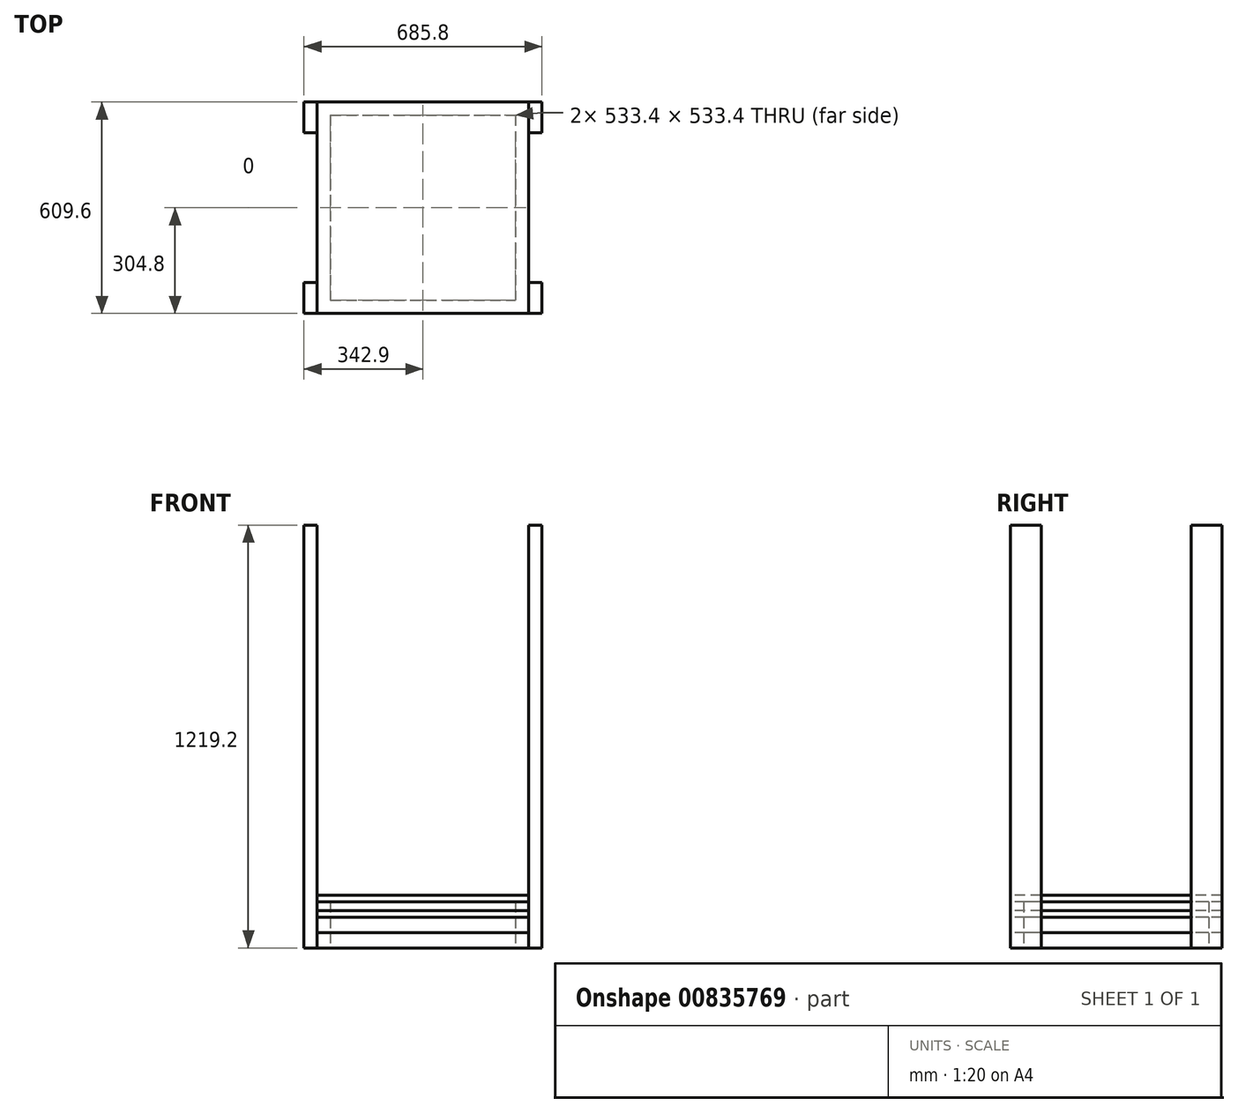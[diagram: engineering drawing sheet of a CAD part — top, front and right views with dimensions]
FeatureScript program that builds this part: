
annotation { "Feature Type Name" : "Feature", "Feature Type Description" : "" }
export const myFeature = defineFeature(function(context is Context, id is Id, definition is map)
    precondition{}
    {
        {
            var Q0;
            Q0=qCreatedBy(makeId("Top.planeOp"),FACE);
            var sketch = newSketch(context, id + "F0", { "sketchPlane" : qUnion([Q0])});
            skLineSegment(sketch, "E0.top", {"start": v(304.8, -304.8) * mm, "end": v(-304.8, -304.8) * mm, "construction": true});
            skPoint(sketch, "E0.middle", {"position": v(0, 0) * mm});
            skLineSegment(sketch, "E1.bottom", {"start": v(-304.8, 304.8) * mm, "end": v(304.8, 304.8) * mm});
            skLineSegment(sketch, "E1.top", {"start": v(-266.7, 266.7) * mm, "end": v(266.7, 266.7) * mm});
            skLineSegment(sketch, "E2.0.1.0", {"start": v(-266.7, -266.7) * mm, "end": v(266.7, -266.7) * mm});
            skLineSegment(sketch, "E2.0.1.3", {"start": v(-304.8, -304.8) * mm, "end": v(304.8, -304.8) * mm});
            skLineSegment(sketch, "E2.1.0.0", {"start": v(-279.4, 304.8) * mm, "end": v(304.8, 304.8) * mm});
            skLineSegment(sketch, "E2.1.1.0", {"start": v(-266.7, -266.7) * mm, "end": v(304.8, -266.7) * mm});
            skLineSegment(sketch, "E2.1.1.3", {"start": v(-279.4, -304.8) * mm, "end": v(304.8, -304.8) * mm});
            skPoint(sketch, "E3.orphan", {"position": v(330.2, 266.7) * mm});
            skPoint(sketch, "E4.orphan", {"position": v(330.2, -304.8) * mm});
            skLineSegment(sketch, "E5.bottom", {"start": v(-304.8, 304.8) * mm, "end": v(-266.7, 304.8) * mm});
            skLineSegment(sketch, "E5.left", {"start": v(-304.8, 215.9) * mm, "end": v(-304.8, -215.9) * mm});
            skLineSegment(sketch, "E5.right", {"start": v(-266.7, 266.7) * mm, "end": v(-266.7, -266.7) * mm});
            skLineSegment(sketch, "E6.MirrorCS", {"start": v(266.7, 266.7) * mm, "end": v(266.7, -266.7) * mm});
            skLineSegment(sketch, "E7.MirrorCS", {"start": v(304.8, 215.9) * mm, "end": v(304.8, -215.9) * mm});
            skPoint(sketch, "E8.orphan", {"position": v(266.7, 304.8) * mm});
            skPoint(sketch, "E9.orphan", {"position": v(304.8, 304.8) * mm});
            skPoint(sketch, "E10.orphan", {"position": v(304.8, -266.7) * mm});
            skPoint(sketch, "E11.orphan", {"position": v(-304.8, -266.7) * mm});
            skLineSegment(sketch, "E12", {"start": v(-304.8, 304.8) * mm, "end": v(-304.8, 215.9) * mm});
            skLineSegment(sketch, "E13", {"start": v(-304.8, -215.9) * mm, "end": v(-304.8, -304.8) * mm});
            skLineSegment(sketch, "E14", {"start": v(304.8, -215.9) * mm, "end": v(304.8, -304.8) * mm});
            skLineSegment(sketch, "E15", {"start": v(304.8, 304.8) * mm, "end": v(304.8, 215.9) * mm});
            skPoint(sketch, "E16.right.end.orphan", {"position": v(-342.9, 215.9) * mm});
            skPoint(sketch, "E16.right.start.orphan", {"position": v(-342.9, 304.8) * mm});
            skPoint(sketch, "E17.MirrorCS.end.orphan", {"position": v(-342.9, -215.9) * mm});
            skPoint(sketch, "E18.MirrorCS.start.orphan", {"position": v(-342.9, -304.8) * mm});
            skPoint(sketch, "E19.MirrorCS.start.orphan", {"position": v(-304.8, -304.8) * mm});
            skPoint(sketch, "E20.MirrorCS.end.orphan", {"position": v(342.9, -215.9) * mm});
            skPoint(sketch, "E20.MirrorCS.start.orphan", {"position": v(342.9, -304.8) * mm});
            skPoint(sketch, "E21.orphan", {"position": v(304.8, -304.8) * mm});
            skPoint(sketch, "E22.MirrorCS.end.orphan", {"position": v(342.9, 304.8) * mm});
            skPoint(sketch, "E23.MirrorCS.end.orphan", {"position": v(342.9, 215.9) * mm});
            skSolve(sketch);
        }
        {
            var Q0;
            Q0=makeQuery(id+"F0.imprint","IMPRINT",FACE,{"disambiguationData":[TD([[makeQuery(id+"F0.imprint","IMPRINT",EDGE,{"derivedFrom":sQuery(id+"F0.wireOp",EDGE,"E1.top")}),1.0]])]});
            extrude(context, id + "F1", {"entities" : qUnion([Q0]), "depth" : 88.9 * mm, "offsetDistance" : 25.4 * mm});
        }
        {
            var Q0;
            Q0=makeQuery(id+"F1.opExtrude","CAP_FACE",FACE,{"disambiguationData":[OSD([sQuery(id+"F0.wireOp",EDGE,"E1.bottom"),sQuery(id+"F0.wireOp",EDGE,"E1.top"),sQuery(id+"F0.wireOp",EDGE,"E2.0.1.0"),sQuery(id+"F0.wireOp",EDGE,"E2.0.1.3"),sQuery(id+"F0.wireOp",EDGE,"E5.left"),sQuery(id+"F0.wireOp",EDGE,"E5.right"),sQuery(id+"F0.wireOp",EDGE,"E6.MirrorCS"),sQuery(id+"F0.wireOp",EDGE,"E7.MirrorCS"),sQuery(id+"F0.wireOp",EDGE,"E12"),sQuery(id+"F0.wireOp",EDGE,"E13"),sQuery(id+"F0.wireOp",EDGE,"E14"),sQuery(id+"F0.wireOp",EDGE,"E15")])],"isStart":false});
            var sketch = newSketch(context, id + "F2", { "sketchPlane" : qUnion([Q0])});
            skLineSegment(sketch, "E24.0", {"start": v(-342.9, 304.8) * mm, "end": v(-342.9, 215.9) * mm});
            skPoint(sketch, "E25.0", {"position": v(-323.85, 215.9) * mm});
            skLineSegment(sketch, "E26.0", {"start": v(-304.8, 215.9) * mm, "end": v(-342.9, 215.9) * mm});
            skPoint(sketch, "E27.0", {"position": v(323.85, 215.9) * mm});
            skLineSegment(sketch, "E28.0", {"start": v(304.8, 215.9) * mm, "end": v(342.9, 215.9) * mm});
            skLineSegment(sketch, "E29.0", {"start": v(342.9, 304.8) * mm, "end": v(342.9, 215.9) * mm});
            skPoint(sketch, "E30.0", {"position": v(323.85, -215.9) * mm});
            skLineSegment(sketch, "E31.0", {"start": v(304.8, -215.9) * mm, "end": v(342.9, -215.9) * mm});
            skLineSegment(sketch, "E32.0", {"start": v(342.9, -304.8) * mm, "end": v(342.9, -215.9) * mm});
            skLineSegment(sketch, "E33.0", {"start": v(-304.8, -215.9) * mm, "end": v(-342.9, -215.9) * mm});
            skLineSegment(sketch, "E34.0", {"start": v(-342.9, -304.8) * mm, "end": v(-342.9, -215.9) * mm});
            skLineSegment(sketch, "E35", {"start": v(-342.9, 304.8) * mm, "end": v(-304.8, 304.8) * mm});
            skLineSegment(sketch, "E36", {"start": v(-304.8, 304.8) * mm, "end": v(-304.8, 215.9) * mm});
            skLineSegment(sketch, "E37", {"start": v(304.8, 215.9) * mm, "end": v(304.8, 304.8) * mm});
            skLineSegment(sketch, "E38", {"start": v(304.8, 304.8) * mm, "end": v(342.9, 304.8) * mm});
            skLineSegment(sketch, "E39", {"start": v(304.8, -215.9) * mm, "end": v(304.8, -304.8) * mm});
            skLineSegment(sketch, "E40", {"start": v(304.8, -304.8) * mm, "end": v(342.9, -304.8) * mm});
            skLineSegment(sketch, "E41", {"start": v(-304.8, -215.9) * mm, "end": v(-304.8, -304.8) * mm});
            skLineSegment(sketch, "E42", {"start": v(-304.8, -304.8) * mm, "end": v(-342.9, -304.8) * mm});
            skSolve(sketch);
        }
        {
            var Q0;
            Q0 = qSketchRegion(id + "F2", true);
            extrude(context, id + "F3", {"entities" : qUnion([Q0]), "depth" : 1130.3 * mm, "offsetDistance" : 25.4 * mm, "hasSecondDirection" : true, "secondDirectionOppositeDirection" : true, "secondDirectionDepth" : 88.9 * mm});
        }
        {
            var Q0;
            Q0=makeQuery(id+"F1.opExtrude","CAP_FACE",FACE,{"disambiguationData":[OSD([sQuery(id+"F0.wireOp",EDGE,"E1.bottom"),sQuery(id+"F0.wireOp",EDGE,"E1.top"),sQuery(id+"F0.wireOp",EDGE,"E2.0.1.0"),sQuery(id+"F0.wireOp",EDGE,"E2.0.1.3"),sQuery(id+"F0.wireOp",EDGE,"E5.left"),sQuery(id+"F0.wireOp",EDGE,"E5.right"),sQuery(id+"F0.wireOp",EDGE,"E6.MirrorCS"),sQuery(id+"F0.wireOp",EDGE,"E7.MirrorCS"),sQuery(id+"F0.wireOp",EDGE,"E12"),sQuery(id+"F0.wireOp",EDGE,"E13"),sQuery(id+"F0.wireOp",EDGE,"E14"),sQuery(id+"F0.wireOp",EDGE,"E15")])],"isStart":false});
            var sketch = newSketch(context, id + "F4", { "sketchPlane" : qUnion([Q0])});
            skLineSegment(sketch, "E43.bottom", {"start": v(304.8, -304.8) * mm, "end": v(-304.8, -304.8) * mm});
            skLineSegment(sketch, "E43.top", {"start": v(304.8, 304.8) * mm, "end": v(-304.8, 304.8) * mm});
            skLineSegment(sketch, "E43.left", {"start": v(304.8, -304.8) * mm, "end": v(304.8, 304.8) * mm});
            skLineSegment(sketch, "E43.right", {"start": v(-304.8, -304.8) * mm, "end": v(-304.8, 304.8) * mm});
            skSolve(sketch);
        }
        {
            var Q0;
            Q0 = qSketchRegion(id + "F4", true);
            extrude(context, id + "F5", {"entities" : qUnion([Q0]), "depth" : 19.05 * mm, "offsetDistance" : 25.4 * mm});
        }
        {
            var Q0;
            Q0=makeQuery(id+"F1.opExtrude","SWEPT_BODY",BODY,{"disambiguationData":[OSD([sQuery(id+"F0.wireOp",EDGE,"E1.bottom"),sQuery(id+"F0.wireOp",EDGE,"E1.top"),sQuery(id+"F0.wireOp",EDGE,"E2.0.1.0"),sQuery(id+"F0.wireOp",EDGE,"E2.0.1.3"),sQuery(id+"F0.wireOp",EDGE,"E5.left"),sQuery(id+"F0.wireOp",EDGE,"E5.right"),sQuery(id+"F0.wireOp",EDGE,"E6.MirrorCS"),sQuery(id+"F0.wireOp",EDGE,"E7.MirrorCS"),sQuery(id+"F0.wireOp",EDGE,"E12"),sQuery(id+"F0.wireOp",EDGE,"E13"),sQuery(id+"F0.wireOp",EDGE,"E14"),sQuery(id+"F0.wireOp",EDGE,"E15")])]});
            var Q1;
            Q1=makeQuery(id+"F5.opExtrude","SWEPT_BODY",BODY,{"disambiguationData":[OSD([sQuery(id+"F4.wireOp",EDGE,"E43.bottom"),sQuery(id+"F4.wireOp",EDGE,"E43.top"),sQuery(id+"F4.wireOp",EDGE,"E43.left"),sQuery(id+"F4.wireOp",EDGE,"E43.right")])]});
            transform(context, id + "F6", {"entities" : qUnion([Q0, Q1]), "transformType" : TransformType.TRANSLATION_3D, "dx" : 0 * mm, "dy" : 0 * mm, "dz" : (48 - (3.5 + 0.75)) * mm, "makeCopy" : true});
        }
    });
